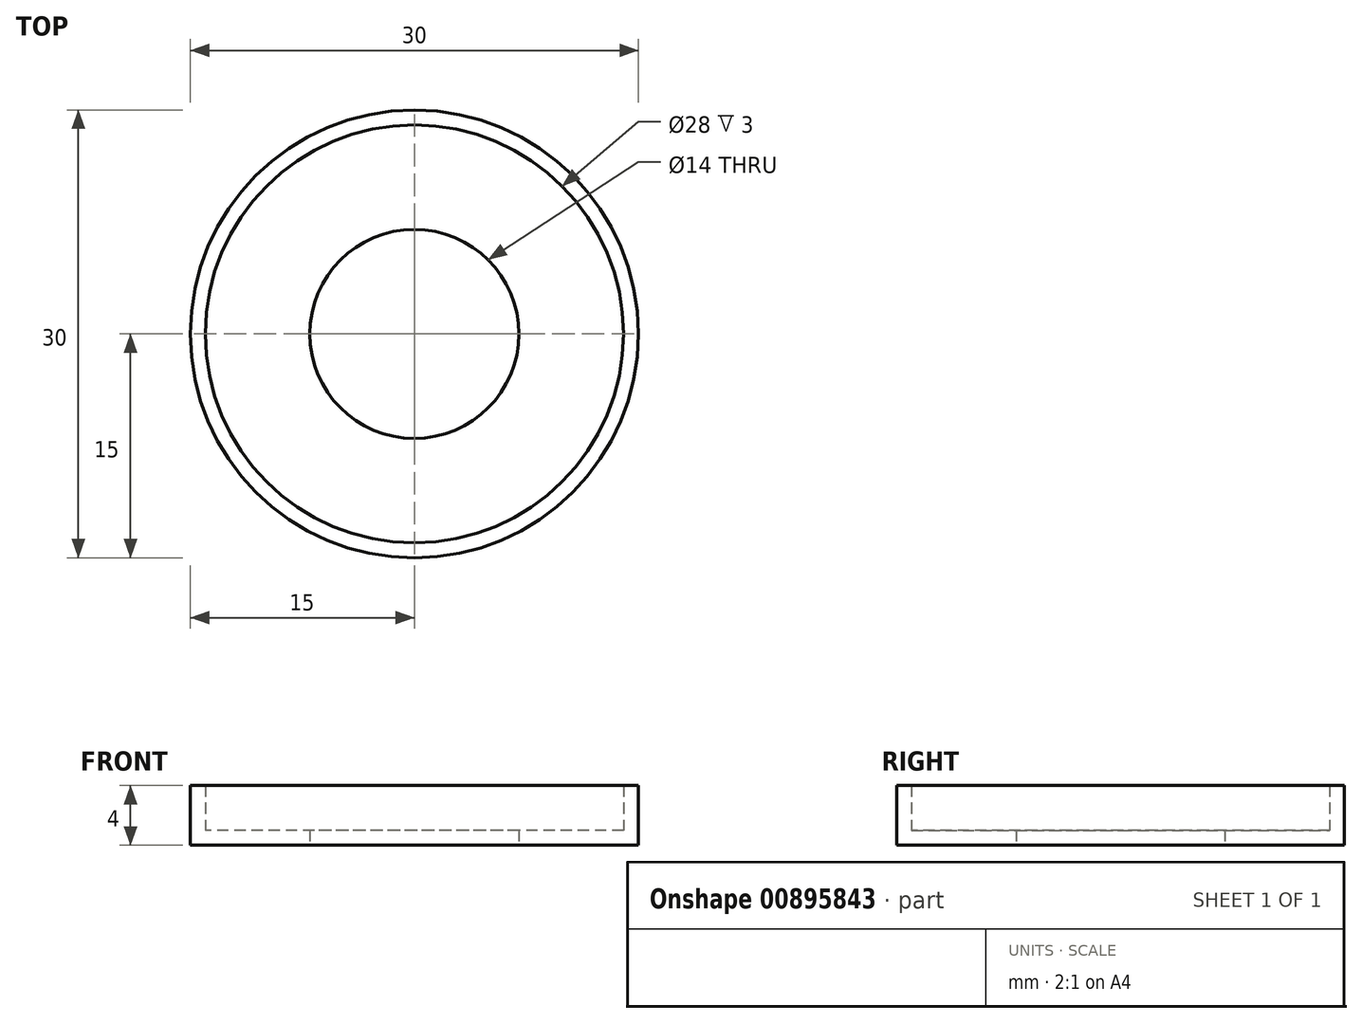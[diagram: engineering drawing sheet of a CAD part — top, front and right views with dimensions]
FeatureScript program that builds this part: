
annotation { "Feature Type Name" : "Feature", "Feature Type Description" : "" }
export const myFeature = defineFeature(function(context is Context, id is Id, definition is map)
    precondition{}
    {
        {
            var Q0;
            Q0=qCreatedBy(makeId("Top.planeOp"),FACE);
            var sketch = newSketch(context, id + "F0", { "sketchPlane" : qUnion([Q0])});
            skCircle(sketch, "E0", {"center": v(0, 0) * mm, "radius": 15 * mm});
            skSolve(sketch);
        }
        {
            var Q0;
            Q0 = qSketchRegion(id + "F0", true);
            extrude(context, id + "F1", {"entities" : qUnion([Q0]), "depth" : 4 * mm, "offsetDistance" : 25 * mm});
        }
        {
            var Q0;
            Q0=makeQuery(id+"F1.opExtrude","CAP_FACE",FACE,{"disambiguationData":[OSD([sQuery(id+"F0.wireOp",EDGE,"E0")])],"isStart":false});
            shell(context, id + "F2", {"entities" : qUnion([Q0]), "thickness" : 1 * mm});
        }
        {
            var Q0;
            Q0=qCreatedBy(makeId("Top.planeOp"),FACE);
            var sketch = newSketch(context, id + "F3", { "sketchPlane" : qUnion([Q0])});
            skCircle(sketch, "E1", {"center": v(0, 0) * mm, "radius": 7 * mm});
            skSolve(sketch);
        }
        {
            var Q0;
            Q0 = qSketchRegion(id + "F3", true);
            extrude(context, id + "F4", {"entities" : qUnion([Q0]), "operationType" : NewBodyOperationType.REMOVE, "depth" : 1.1 * mm, "offsetDistance" : 25 * mm});
        }
    });
